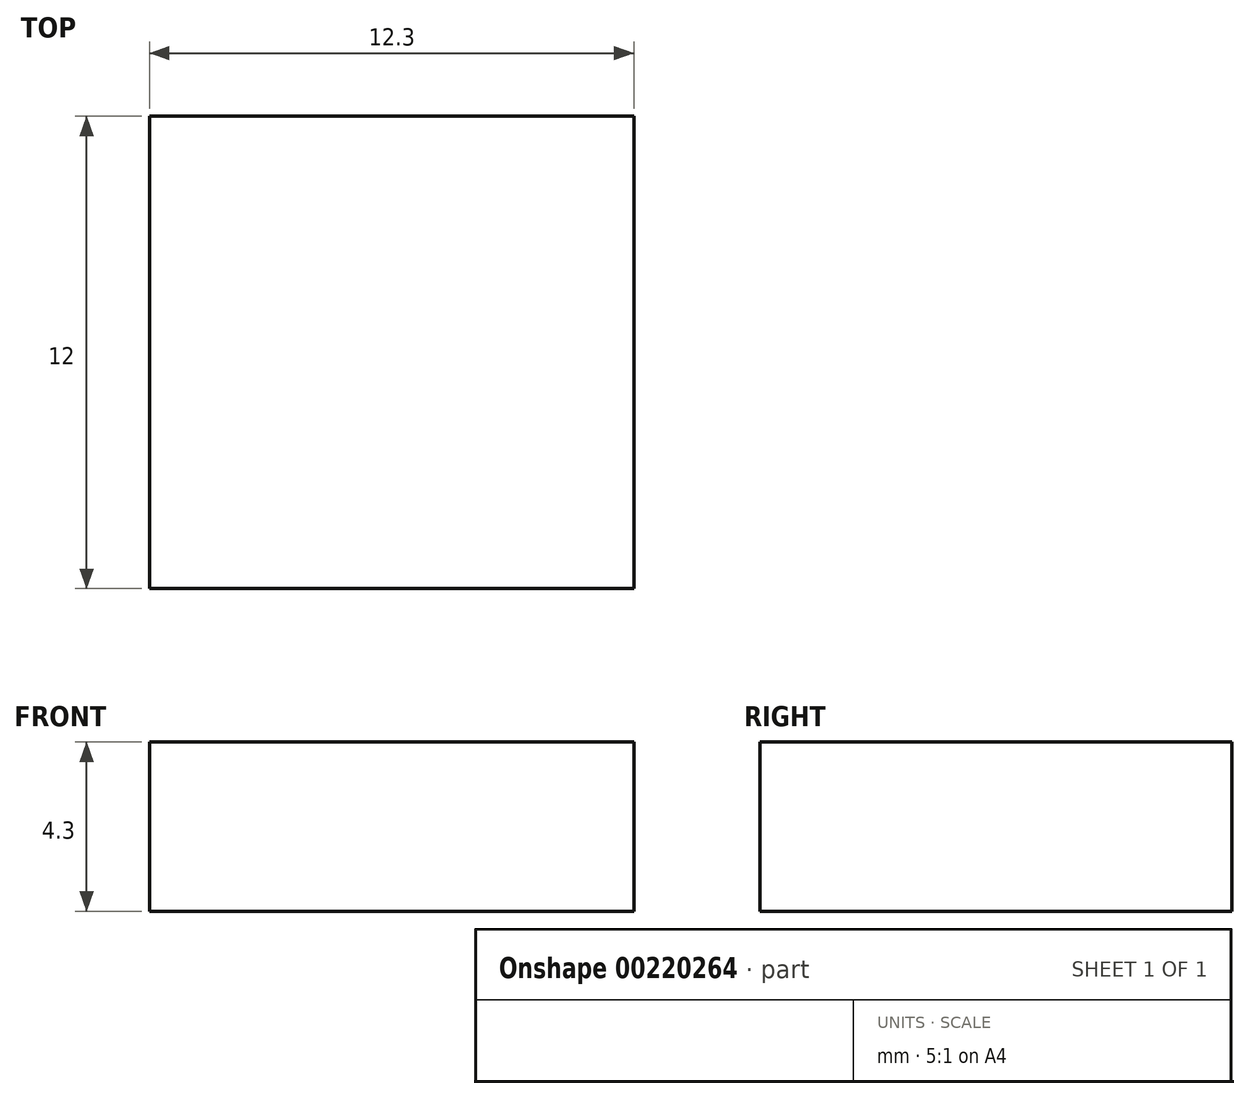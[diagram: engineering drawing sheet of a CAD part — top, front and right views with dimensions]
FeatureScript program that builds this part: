
annotation { "Feature Type Name" : "Feature", "Feature Type Description" : "" }
export const myFeature = defineFeature(function(context is Context, id is Id, definition is map)
    precondition{}
    {
        {
            var Q0;
            Q0=qCreatedBy(makeId("Top.planeOp"),FACE);
            var sketch = newSketch(context, id + "F0", { "sketchPlane" : qUnion([Q0])});
            skLineSegment(sketch, "E0.bottom", {"start": v(6.15, 6) * mm, "end": v(-6.15, 6) * mm});
            skLineSegment(sketch, "E0.top", {"start": v(6.15, -6) * mm, "end": v(-6.15, -6) * mm});
            skLineSegment(sketch, "E0.left", {"start": v(6.15, 6) * mm, "end": v(6.15, -6) * mm});
            skLineSegment(sketch, "E0.right", {"start": v(-6.15, 6) * mm, "end": v(-6.15, -6) * mm});
            skPoint(sketch, "E0.middle", {"position": v(0, 0) * mm});
            skSolve(sketch);
        }
        {
            var Q0;
            Q0=makeQuery(id+"F0.imprint","IMPRINT",FACE,{"disambiguationData":[TD([[makeQuery(id+"F0.imprint","IMPRINT",EDGE,{"derivedFrom":sQuery(id+"F0.wireOp",EDGE,"E0.bottom")}),1.0]])]});
            extrude(context, id + "F1", {"entities" : qUnion([Q0]), "depth" : 4.3 * mm});
        }
    });
